# Revit family: NBS_Allermuir_DmstcChrs_Oran-en-us_Chair
name_source: partatom
category: Furniture
revit_build: Autodesk Revit 2016 (Build: 20151007_0715(x64)
units: mm (PartAtom-declared; Revit-internal decimal feet)

## family parameters
Always vertical = Yes
Cut with Voids When Loaded = No
Room Calculation Point = No
Shared = No
Work Plane-Based = No

## types (1)
- ORA100
    AssetType = Moveable
    BIMObjectName = NBS_Allermuir_DomesticChairs_Oran_ORA100-US
    Category = Pr_40_50_12_22:Dining chairs
    Chair = Yes
    Description = Arm chair
    DurationUnit = year
    ExpectedLife = 10
    Features = Fully upholstered, traditional carcass construction, tensioned seat support, feather wrapped sprung seat foam, cast aluminum legs and aluminum perimeter frame finished in black powder coat, curled feather filled cushion with fire retardant inner cover, plastic glides, aluminum frame available in tusk grey powder coat, wo-tone upholstery
    FrameLength = 36 "
    FramesColour = Black, tusk grey
    FramesFinish = Powder coat
    FramesMaterial = Aluminum
    HighestSeatingHeight = 0 "
    IfcExportAs = IfcFurnitureType
    IfcExportType = SOFA
    IsBuiltIn = No
    LowestSeatingHeight = 0 "
    ManufacturerName = Allermuir
    ManufacturerURL = http://www.thesenatorgroup.com
    ModelNumber = ORA100
    ModelReference = Oran
    NBSCertification = www.nationalbimlibrary.com/cert/ndm0vjjv
    NBSDescription = Domestic chairs
    NBSReference = 45-35-20/365
    Name = DomesticChairs_Oran_ORA100-US_Allermuir
    NominalDepth = 37 "
    NominalHeight = 28 "
    NominalLength = 38 "
    NominalWidth = 38 "
    OmniClassCode = 22-12 52 23
    OmniClassTitle = Office Seating
    OmniClassVersion = Table 22 2012-05-16
    SeatFrameMaterial = NBS_Concept
    SeatSeatingMaterial = NBS_Concept
    SeatingHeight = 17 "
    SeatsAndBacksFinish = Fully upholstered
    Size = 37 x 37.5 x 27.5"
    Status = UNSET
    Uniclass2015Code = Pr_40_50_12_22
    Uniclass2015Title = Dining chairs
    Uniclass2015Version = Products v1.9
    Version = 1
    WarrantyDescription = Allermuir warrant that its manufactured products are free from manufacturing defects in materials or workmanship for a period of ten years
    WarrantyDurationParts = 10
    WarrantyDurationUnit = year

## geometry (parser evidence)
native form markers: Sweep x15
no freeform markers — native parametric forms only
